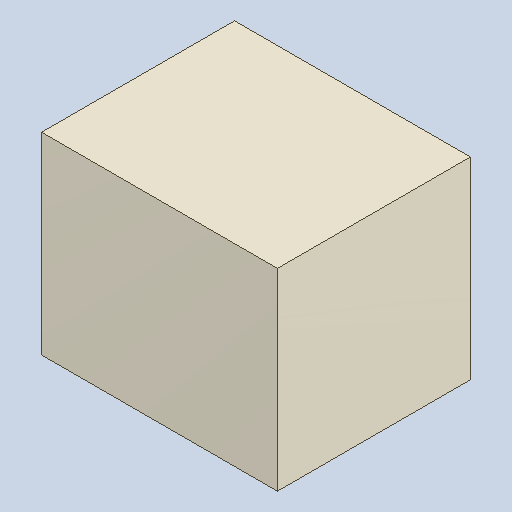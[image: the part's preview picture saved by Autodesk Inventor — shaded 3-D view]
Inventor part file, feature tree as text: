
AUTODESK INVENTOR PART (.ipt)
format: ipt  version: 2023.4 (Build 274418000, 418)  size: 81,920 bytes
history: native  units: mm
features: extrude x1
ambient origin geometry x8: Origin, YZ Plane, XZ Plane, XY Plane, X Axis, Y Axis, Z Axis, Center Point
bodies: Solid1 (feature_tree)
feature tree (1):
  extrude  "Extruded_8"  [1 undecoded]
note: 1 required parameter value undecoded (feature->parameter linkage not recoverable at this tier; creation-order binding heuristic only, values carry confidence <= 0.55)
